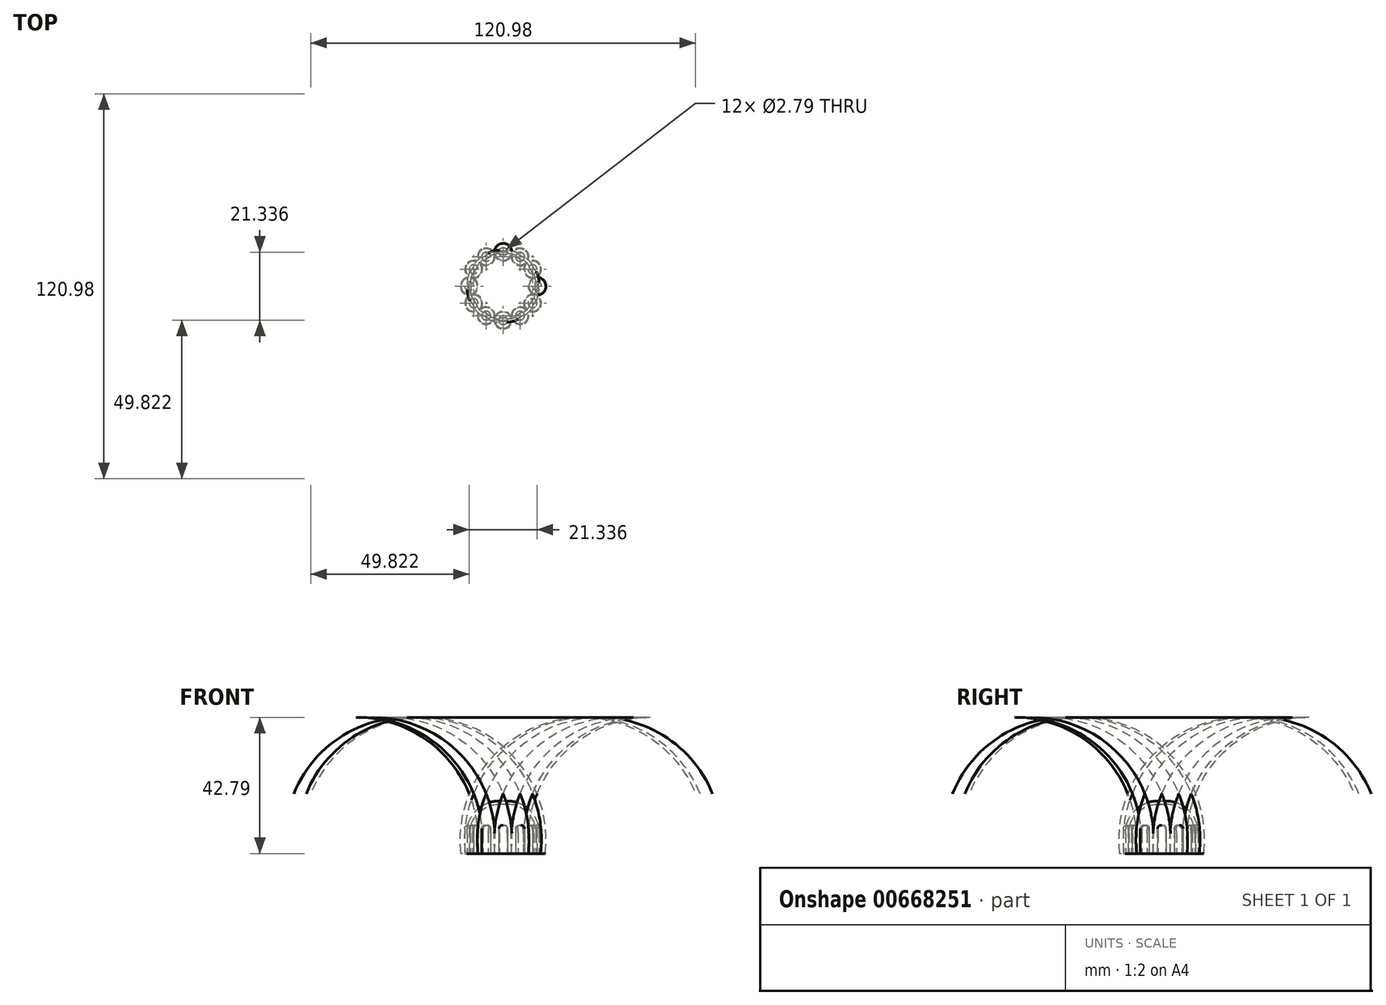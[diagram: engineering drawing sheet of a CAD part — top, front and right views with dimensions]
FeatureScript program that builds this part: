
annotation { "Feature Type Name" : "Feature", "Feature Type Description" : "" }
export const myFeature = defineFeature(function(context is Context, id is Id, definition is map)
    precondition{}
    {
        {
            var Q0;
            Q0=qCreatedBy(makeId("Top.planeOp"),FACE);
            var sketch = newSketch(context, id + "F0", { "sketchPlane" : qUnion([Q0])});
            skCircle(sketch, "E0", {"center": v(0, 0) * mm, "radius": 11.43 * mm});
            skCircle(sketch, "E1", {"center": v(-25.4, 0) * mm, "radius": 12.7 * mm});
            skLineSegment(sketch, "E2", {"start": v(-21.64, 12.13) * mm, "end": v(0, 0) * mm});
            skLineSegment(sketch, "E3", {"start": v(-21.64, -12.13) * mm, "end": v(0, 0) * mm});
            skLineSegment(sketch, "E4", {"start": v(0, 0) * mm, "end": v(0, -17.88) * mm, "construction": true});
            skCircle(sketch, "E5", {"center": v(0, 11.43) * mm, "radius": 2.16 * mm});
            skSolve(sketch);
        }
        {
            var Q0;
            {var subQ0=sQuery(id+"F0.wireOp",EDGE,"E2");var subQ1=sQuery(id+"F0.wireOp",EDGE,"E0");var subQ2=makeQuery(id+"F0.imprint","INTERSECT",VERTEX,{"derivedFrom":[subQ1,subQ0]});Q0=makeQuery(id+"F0.imprint","IMPRINT",FACE,{"disambiguationData":[TD([[makeQuery(id+"F0.imprint","IMPRINT",EDGE,{"disambiguationData":[TD([[subQ2,1.0]])],"derivedFrom":subQ1}),1.0]])]});}
            var Q1;
            {var subQ0=sQuery(id+"F0.wireOp",EDGE,"E2");var subQ1=sQuery(id+"F0.wireOp",EDGE,"E0");var subQ2=makeQuery(id+"F0.imprint","INTERSECT",VERTEX,{"derivedFrom":[subQ1,subQ0]});Q1=makeQuery(id+"F0.imprint","IMPRINT",FACE,{"disambiguationData":[TD([[makeQuery(id+"F0.imprint","IMPRINT",EDGE,{"disambiguationData":[TD([[subQ2,-1.0]])],"derivedFrom":subQ1}),1.0]])]});}
            var Q2;
            {var subQ0=sQuery(id+"F0.wireOp",EDGE,"E5");var subQ1=sQuery(id+"F0.wireOp",EDGE,"E0");var subQ2=makeQuery(id+"F0.imprint","INTERSECT",VERTEX,{"disambiguationData":[OD(0.0)],"derivedFrom":[subQ1,subQ0]});Q2=makeQuery(id+"F0.imprint","IMPRINT",FACE,{"disambiguationData":[TD([[makeQuery(id+"F0.imprint","IMPRINT",EDGE,{"disambiguationData":[TD([[subQ2,1.0]])],"derivedFrom":subQ1}),1.0]])]});}
            var Q3;
            {var subQ0=sQuery(id+"F0.wireOp",EDGE,"E1");var subQ1=sQuery(id+"F0.wireOp",EDGE,"E0");var subQ2=makeQuery(id+"F0.imprint","INTERSECT",VERTEX,{"disambiguationData":[OD(0.0)],"derivedFrom":[subQ1,subQ0]});Q3=makeQuery(id+"F0.imprint","IMPRINT",FACE,{"disambiguationData":[TD([[makeQuery(id+"F0.imprint","IMPRINT",EDGE,{"disambiguationData":[TD([[subQ2,-1.0]])],"derivedFrom":subQ1}),1.0]])]});}
            extrude(context, id + "F1", {"entities" : qUnion([Q0, Q1, Q2, Q3]), "depth" : 16.5 * mm});
        }
        {
            var Q0;
            {var subQ0=makeQuery(id+"Fn2lx3xh9olqKXz_0.opExtrude","SWEPT_FACE",FACE,{"disambiguationData":[OSD([sQuery(id+"F0.wireOp",EDGE,"E2")])]});var subQ1=sQuery(id+"F0.wireOp",EDGE,"E0");Q0=makeQuery(id+"F1.boolean.opBoolean","SPLIT",EDGE,{"disambiguationData":[TD([subQ0])],"derivedFrom":makeQuery(id+"F1.opExtrude","CAP_EDGE",EDGE,{"disambiguationData":[OSD([subQ1])],"isStart":false})});}
            fillet(context, id + "F2", {"entities" : qUnion([Q0]), "radius" : 10.16 * mm, "allowEdgeOverflow" : false});
        }
        {
            var Q0;
            Q0=makeQuery(id+"F1.opExtrude","CAP_FACE",FACE,{"disambiguationData":[OSD([sQuery(id+"F0.wireOp",EDGE,"E0")])],"isStart":true});
            shell(context, id + "F3", {"entities" : qUnion([Q0]), "thickness" : 1.02 * mm});
        }
        {
            var Q0;
            Q0=qCreatedBy(makeId("Front.planeOp"),FACE);
            var sketch = newSketch(context, id + "F4", { "sketchPlane" : qUnion([Q0])});
            skLineSegment(sketch, "E6", {"start": v(0, 0) * mm, "end": v(0, 40.39) * mm});
            skArc(sketch, "E7", {"start": v(2.54, 0) * mm, "mid": v(2.45, 9.56) * mm, "end": v(0, 18.8) * mm});
            skLineSegment(sketch, "E8", {"start": v(0, 0) * mm, "end": v(2.54, 0) * mm});
            skSolve(sketch);
        }
        {
            var Q0;
            {var subQ2=sQuery(id+"F4.wireOp",EDGE,"E7");Q0=makeQuery(id+"F4.imprint","IMPRINT",FACE,{"disambiguationData":[TD([[makeQuery(id+"F4.imprint","IMPRINT",EDGE,{"derivedFrom":subQ2}),1.0]])]});}
            var Q1;
            Q1=sQuery(id+"F4.wireOp",EDGE,"E6");
            revolve(context, id + "F5", {"entities" : qUnion([Q0]), "axis" : qUnion([Q1]), "revolveType" : RevolveType.FULL});
        }
        {
            var Q0;
            Q0=makeQuery(id+"F5.opRevolve","SWEPT_BODY",BODY,{"disambiguationData":[OSD([sQuery(id+"F4.wireOp",EDGE,"E6"),sQuery(id+"F4.wireOp",EDGE,"E7"),sQuery(id+"F4.wireOp",EDGE,"E8")])]});
            transform(context, id + "F6", {"entities" : qUnion([Q0]), "transformType" : TransformType.TRANSLATION_3D, "dx" : 10.67 * mm, "dy" : 0 * mm, "dz" : 0 * mm, "makeCopy" : false});
        }
        {
            var Q0;
            Q0=makeQuery(id+"F5.opRevolve","SWEPT_BODY",BODY,{"disambiguationData":[OSD([sQuery(id+"F4.wireOp",EDGE,"E6"),sQuery(id+"F4.wireOp",EDGE,"E7"),sQuery(id+"F4.wireOp",EDGE,"E8")])]});
            var Q1;
            Q1=makeQuery(id+"F1.opExtrude","CAP_EDGE",EDGE,{"disambiguationData":[OSD([sQuery(id+"F0.wireOp",EDGE,"E0")])],"isStart":true});
            circularPattern(context, id + "F7", {"entities" : qUnion([Q0]), "axis" : qUnion([Q1]), "angle" : 360 * degree, "instanceCount" : 12, "equalSpace" : true});
        }
        {
            var Q0;
            Q0=qCreatedBy(makeId("Top.planeOp"),FACE);
            var sketch = newSketch(context, id + "F8", { "sketchPlane" : qUnion([Q0])});
            skCircle(sketch, "E9", {"center": v(0, 0) * mm, "radius": 1.4 * mm});
            skSolve(sketch);
        }
        {
            var Q0;
            Q0=makeQuery(id+"F8.imprint","IMPRINT",FACE,{"disambiguationData":[TD([[makeQuery(id+"F8.imprint","IMPRINT",EDGE,{"derivedFrom":sQuery(id+"F8.wireOp",EDGE,"E9")}),1.0]])]});
            extrude(context, id + "F9", {"entities" : qUnion([Q0]), "endBound" : BoundingType.SYMMETRIC, "depth" : 17.78 * mm});
        }
        {
            var Q0;
            Q0=makeQuery(id+"F9.opExtrude","CAP_EDGE",EDGE,{"disambiguationData":[OSD([sQuery(id+"F8.wireOp",EDGE,"E9")])],"isStart":false});
            fillet(context, id + "F10", {"entities" : qUnion([Q0]), "radius" : 1.02 * mm, "tangentPropagation" : true, "allowEdgeOverflow" : false});
        }
        {
            var Q0;
            Q0=makeQuery(id+"F9.opExtrude","SWEPT_BODY",BODY,{"disambiguationData":[OSD([sQuery(id+"F8.wireOp",EDGE,"E9")])]});
            transform(context, id + "F11", {"entities" : qUnion([Q0]), "transformType" : TransformType.TRANSLATION_3D, "dx" : 10.67 * mm, "dy" : 0 * mm, "dz" : 0 * mm, "makeCopy" : false});
        }
        {
            var Q0;
            Q0=makeQuery(id+"F9.opExtrude","SWEPT_BODY",BODY,{"disambiguationData":[OSD([sQuery(id+"F8.wireOp",EDGE,"E9")])]});
            var Q1;
            Q1=makeQuery(id+"F1.opExtrude","CAP_EDGE",EDGE,{"disambiguationData":[OSD([sQuery(id+"F0.wireOp",EDGE,"E0")])],"isStart":true});
            circularPattern(context, id + "F12", {"entities" : qUnion([Q0]), "axis" : qUnion([Q1]), "angle" : 360 * degree, "instanceCount" : 12, "equalSpace" : true});
        }
        {
            var Q0;
            Q0=makeQuery(id+"F12.opPattern","COPY",BODY,{"derivedFrom":makeQuery(id+"F9.opExtrude","SWEPT_BODY",BODY,{"disambiguationData":[OSD([sQuery(id+"F8.wireOp",EDGE,"E9")])]}),"instanceName":"9"});
            var Q1;
            Q1=makeQuery(id+"F12.opPattern","COPY",BODY,{"derivedFrom":makeQuery(id+"F9.opExtrude","SWEPT_BODY",BODY,{"disambiguationData":[OSD([sQuery(id+"F8.wireOp",EDGE,"E9")])]}),"instanceName":"10"});
            var Q2;
            Q2=makeQuery(id+"F12.opPattern","COPY",BODY,{"derivedFrom":makeQuery(id+"F9.opExtrude","SWEPT_BODY",BODY,{"disambiguationData":[OSD([sQuery(id+"F8.wireOp",EDGE,"E9")])]}),"instanceName":"11"});
            var Q3;
            Q3=makeQuery(id+"F9.opExtrude","SWEPT_BODY",BODY,{"disambiguationData":[OSD([sQuery(id+"F8.wireOp",EDGE,"E9")])]});
            var Q4;
            Q4=makeQuery(id+"F12.opPattern","COPY",BODY,{"derivedFrom":makeQuery(id+"F9.opExtrude","SWEPT_BODY",BODY,{"disambiguationData":[OSD([sQuery(id+"F8.wireOp",EDGE,"E9")])]}),"instanceName":"1"});
            var Q5;
            Q5=makeQuery(id+"F12.opPattern","COPY",BODY,{"derivedFrom":makeQuery(id+"F9.opExtrude","SWEPT_BODY",BODY,{"disambiguationData":[OSD([sQuery(id+"F8.wireOp",EDGE,"E9")])]}),"instanceName":"2"});
            var Q6;
            Q6=makeQuery(id+"F12.opPattern","COPY",BODY,{"derivedFrom":makeQuery(id+"F9.opExtrude","SWEPT_BODY",BODY,{"disambiguationData":[OSD([sQuery(id+"F8.wireOp",EDGE,"E9")])]}),"instanceName":"3"});
            var Q7;
            Q7=makeQuery(id+"F12.opPattern","COPY",BODY,{"derivedFrom":makeQuery(id+"F9.opExtrude","SWEPT_BODY",BODY,{"disambiguationData":[OSD([sQuery(id+"F8.wireOp",EDGE,"E9")])]}),"instanceName":"4"});
            var Q8;
            Q8=makeQuery(id+"F12.opPattern","COPY",BODY,{"derivedFrom":makeQuery(id+"F9.opExtrude","SWEPT_BODY",BODY,{"disambiguationData":[OSD([sQuery(id+"F8.wireOp",EDGE,"E9")])]}),"instanceName":"5"});
            var Q9;
            Q9=makeQuery(id+"F12.opPattern","COPY",BODY,{"derivedFrom":makeQuery(id+"F9.opExtrude","SWEPT_BODY",BODY,{"disambiguationData":[OSD([sQuery(id+"F8.wireOp",EDGE,"E9")])]}),"instanceName":"6"});
            var Q10;
            Q10=makeQuery(id+"F12.opPattern","COPY",BODY,{"derivedFrom":makeQuery(id+"F9.opExtrude","SWEPT_BODY",BODY,{"disambiguationData":[OSD([sQuery(id+"F8.wireOp",EDGE,"E9")])]}),"instanceName":"7"});
            var Q11;
            Q11=makeQuery(id+"F12.opPattern","COPY",BODY,{"derivedFrom":makeQuery(id+"F9.opExtrude","SWEPT_BODY",BODY,{"disambiguationData":[OSD([sQuery(id+"F8.wireOp",EDGE,"E9")])]}),"instanceName":"8"});
            var Q12;
            Q12=makeQuery(id+"F1.opExtrude","SWEPT_BODY",BODY,{"disambiguationData":[OSD([sQuery(id+"F0.wireOp",EDGE,"E0")])]});
            var Q13;
            Q13=makeQuery(id+"F7.opPattern","COPY",BODY,{"derivedFrom":makeQuery(id+"F5.opRevolve","SWEPT_BODY",BODY,{"disambiguationData":[OSD([sQuery(id+"F4.wireOp",EDGE,"E6"),sQuery(id+"F4.wireOp",EDGE,"E7"),sQuery(id+"F4.wireOp",EDGE,"E8")])]}),"instanceName":"3"});
            var Q14;
            Q14=makeQuery(id+"F7.opPattern","COPY",BODY,{"derivedFrom":makeQuery(id+"F5.opRevolve","SWEPT_BODY",BODY,{"disambiguationData":[OSD([sQuery(id+"F4.wireOp",EDGE,"E6"),sQuery(id+"F4.wireOp",EDGE,"E7"),sQuery(id+"F4.wireOp",EDGE,"E8")])]}),"instanceName":"2"});
            var Q15;
            Q15=makeQuery(id+"F7.opPattern","COPY",BODY,{"derivedFrom":makeQuery(id+"F5.opRevolve","SWEPT_BODY",BODY,{"disambiguationData":[OSD([sQuery(id+"F4.wireOp",EDGE,"E6"),sQuery(id+"F4.wireOp",EDGE,"E7"),sQuery(id+"F4.wireOp",EDGE,"E8")])]}),"instanceName":"1"});
            var Q16;
            Q16=makeQuery(id+"F5.opRevolve","SWEPT_BODY",BODY,{"disambiguationData":[OSD([sQuery(id+"F4.wireOp",EDGE,"E6"),sQuery(id+"F4.wireOp",EDGE,"E7"),sQuery(id+"F4.wireOp",EDGE,"E8")])]});
            var Q17;
            Q17=makeQuery(id+"F7.opPattern","COPY",BODY,{"derivedFrom":makeQuery(id+"F5.opRevolve","SWEPT_BODY",BODY,{"disambiguationData":[OSD([sQuery(id+"F4.wireOp",EDGE,"E6"),sQuery(id+"F4.wireOp",EDGE,"E7"),sQuery(id+"F4.wireOp",EDGE,"E8")])]}),"instanceName":"11"});
            var Q18;
            Q18=makeQuery(id+"F7.opPattern","COPY",BODY,{"derivedFrom":makeQuery(id+"F5.opRevolve","SWEPT_BODY",BODY,{"disambiguationData":[OSD([sQuery(id+"F4.wireOp",EDGE,"E6"),sQuery(id+"F4.wireOp",EDGE,"E7"),sQuery(id+"F4.wireOp",EDGE,"E8")])]}),"instanceName":"10"});
            var Q19;
            Q19=makeQuery(id+"F7.opPattern","COPY",BODY,{"derivedFrom":makeQuery(id+"F5.opRevolve","SWEPT_BODY",BODY,{"disambiguationData":[OSD([sQuery(id+"F4.wireOp",EDGE,"E6"),sQuery(id+"F4.wireOp",EDGE,"E7"),sQuery(id+"F4.wireOp",EDGE,"E8")])]}),"instanceName":"9"});
            var Q20;
            Q20=makeQuery(id+"F7.opPattern","COPY",BODY,{"derivedFrom":makeQuery(id+"F5.opRevolve","SWEPT_BODY",BODY,{"disambiguationData":[OSD([sQuery(id+"F4.wireOp",EDGE,"E6"),sQuery(id+"F4.wireOp",EDGE,"E7"),sQuery(id+"F4.wireOp",EDGE,"E8")])]}),"instanceName":"8"});
            var Q21;
            Q21=makeQuery(id+"F7.opPattern","COPY",BODY,{"derivedFrom":makeQuery(id+"F5.opRevolve","SWEPT_BODY",BODY,{"disambiguationData":[OSD([sQuery(id+"F4.wireOp",EDGE,"E6"),sQuery(id+"F4.wireOp",EDGE,"E7"),sQuery(id+"F4.wireOp",EDGE,"E8")])]}),"instanceName":"7"});
            var Q22;
            Q22=makeQuery(id+"F7.opPattern","COPY",BODY,{"derivedFrom":makeQuery(id+"F5.opRevolve","SWEPT_BODY",BODY,{"disambiguationData":[OSD([sQuery(id+"F4.wireOp",EDGE,"E6"),sQuery(id+"F4.wireOp",EDGE,"E7"),sQuery(id+"F4.wireOp",EDGE,"E8")])]}),"instanceName":"6"});
            var Q23;
            Q23=makeQuery(id+"F7.opPattern","COPY",BODY,{"derivedFrom":makeQuery(id+"F5.opRevolve","SWEPT_BODY",BODY,{"disambiguationData":[OSD([sQuery(id+"F4.wireOp",EDGE,"E6"),sQuery(id+"F4.wireOp",EDGE,"E7"),sQuery(id+"F4.wireOp",EDGE,"E8")])]}),"instanceName":"5"});
            var Q24;
            Q24=makeQuery(id+"F7.opPattern","COPY",BODY,{"derivedFrom":makeQuery(id+"F5.opRevolve","SWEPT_BODY",BODY,{"disambiguationData":[OSD([sQuery(id+"F4.wireOp",EDGE,"E6"),sQuery(id+"F4.wireOp",EDGE,"E7"),sQuery(id+"F4.wireOp",EDGE,"E8")])]}),"instanceName":"4"});
            booleanBodies(context, id + "F13", {"operationType" : BooleanOperationType.SUBTRACTION, "tools" : qUnion([Q0, Q1, Q2, Q3, Q4, Q5, Q6, Q7, Q8, Q9, Q10, Q11]), "targets" : qUnion([Q12, Q13, Q14, Q15, Q16, Q17, Q18, Q19, Q20, Q21, Q22, Q23, Q24])});
        }
    });
